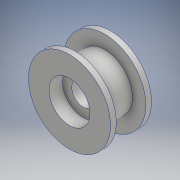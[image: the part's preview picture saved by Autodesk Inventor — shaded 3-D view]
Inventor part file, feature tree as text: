
AUTODESK INVENTOR PART (.ipt)
format: ipt  version: 2017.3 (Build 213256000, 256)  size: 138,240 bytes
history: native  units: mm
features: sketch x2, revolve x1, extrude x1, mirror x1
ambient origin geometry x8: Origin, YZ Plane, XZ Plane, XY Plane, X Axis, Y Axis, Z Axis, Center Point
bodies: Solid1 (feature_tree)
feature tree (5):
  revolve  "Revolution1"  [1 undecoded]
  extrude  "Extrusion1"  Depth=9.0mm
  mirror  "Mirror1"
  sketch  "Sketch1"  dims[d0=2.5mm d1=6.5mm]
  sketch  "Sketch2"  dims[d2=9.0mm d3=9.0mm d4=6.05mm d5=90.0deg d6=9.0mm d7=3.0mm d8=0.0mm]
note: 1 required parameter value undecoded (feature->parameter linkage not recoverable at this tier; creation-order binding heuristic only, values carry confidence <= 0.55)
